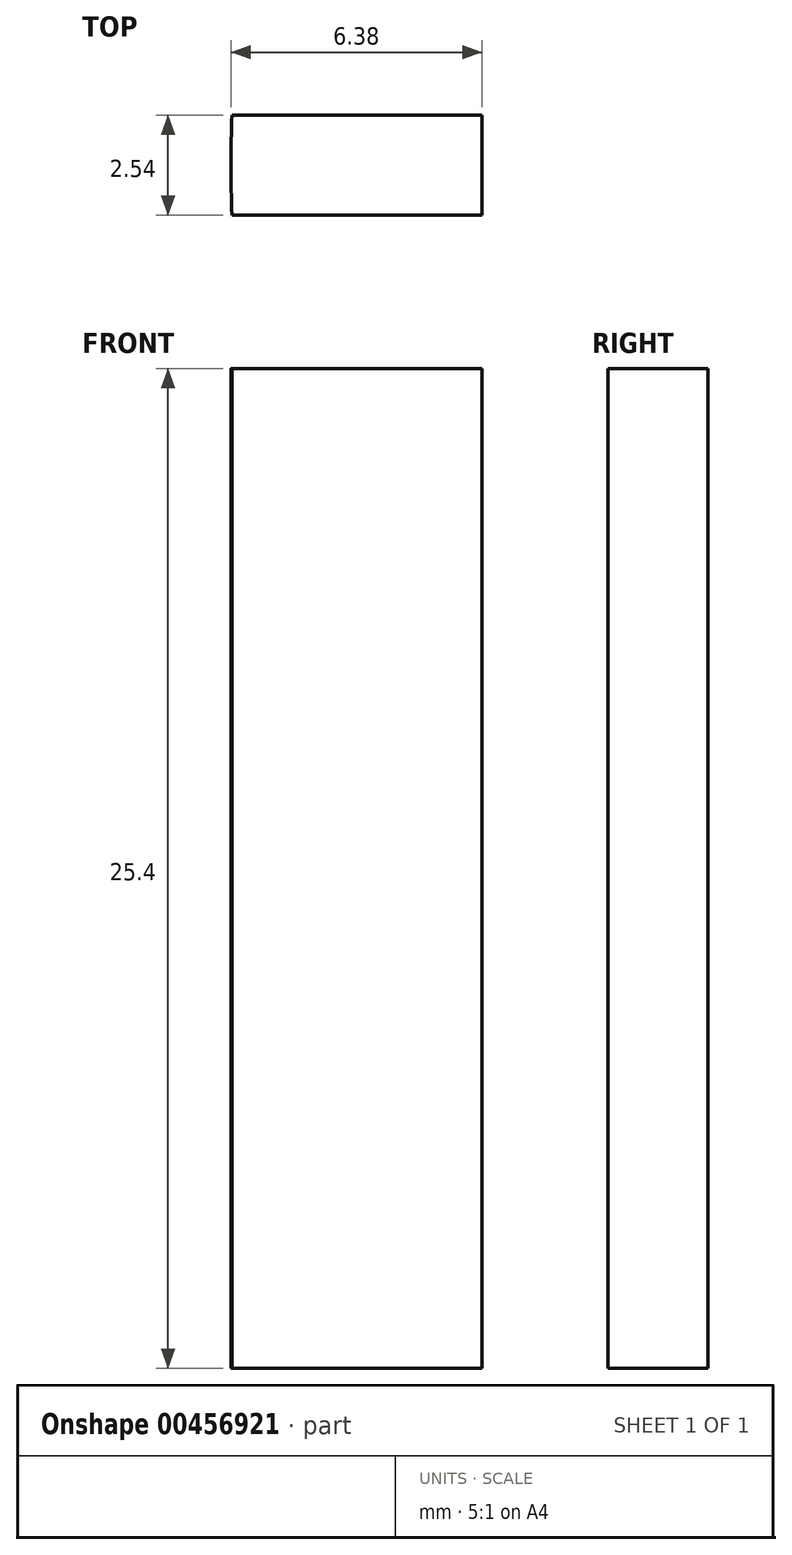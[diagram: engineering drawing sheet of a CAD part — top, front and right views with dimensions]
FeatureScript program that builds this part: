
annotation { "Feature Type Name" : "Feature", "Feature Type Description" : "" }
export const myFeature = defineFeature(function(context is Context, id is Id, definition is map)
    precondition{}
    {
        {
            var Q0;
            Q0=qCreatedBy(makeId("Top.planeOp"),FACE);
            var sketch = newSketch(context, id + "F0", { "sketchPlane" : qUnion([Q0])});
            skCircle(sketch, "E0", {"center": v(0, 0) * mm, "radius": 31.75 * mm});
            skLineSegment(sketch, "E1", {"start": v(-31.72, 1.27) * mm, "end": v(-25.37, 1.27) * mm});
            skLineSegment(sketch, "E2", {"start": v(-25.37, -1.27) * mm, "end": v(-31.72, -1.27) * mm});
            skLineSegment(sketch, "E3", {"start": v(-25.37, 1.27) * mm, "end": v(-25.37, -1.27) * mm});
            skSolve(sketch);
        }
        {
            var Q0;
            {var subQ0=sQuery(id+"F0.wireOp",EDGE,"E1");Q0=makeQuery(id+"F0.imprint","IMPRINT",FACE,{"disambiguationData":[TD([[makeQuery(id+"F0.imprint","IMPRINT",EDGE,{"derivedFrom":subQ0}),-1.0]])]});}
            extrude(context, id + "F1", {"entities" : qUnion([Q0]), "depth" : 25.4 * mm});
        }
    });
